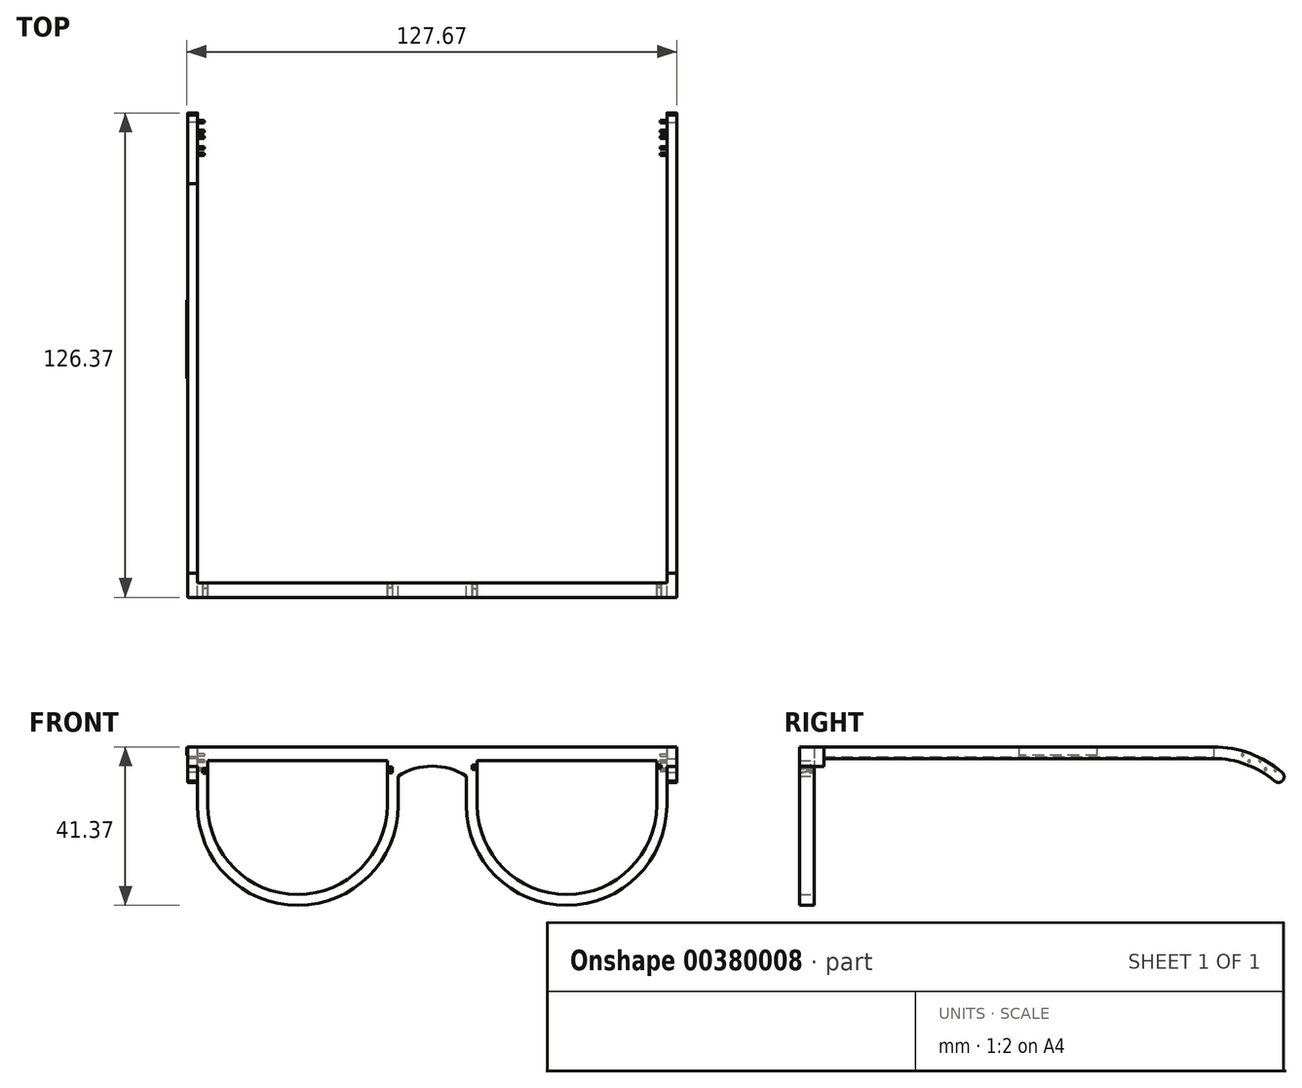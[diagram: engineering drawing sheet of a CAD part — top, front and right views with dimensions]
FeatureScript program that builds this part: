
annotation { "Feature Type Name" : "Feature", "Feature Type Description" : "" }
export const myFeature = defineFeature(function(context is Context, id is Id, definition is map)
    precondition{}
    {
        {
            var Q0;
            Q0=qCreatedBy(makeId("Front.planeOp"),FACE);
            var sketch = newSketch(context, id + "F0", { "sketchPlane" : qUnion([Q0])});
            skLineSegment(sketch, "E0.MirrorCS", {"start": v(0, 35.5) * mm, "end": v(-61.17, 35.5) * mm});
            skArc(sketch, "E1.MirrorCS", {"start": v(-8.9, 20.26) * mm, "mid": v(-35.03, -5.88) * mm, "end": v(-61.17, 20.26) * mm});
            skLineSegment(sketch, "E2.MirrorCS", {"start": v(-61.17, 35.5) * mm, "end": v(-61.17, 20.26) * mm});
            skArc(sketch, "E3", {"start": v(-58.5, 20.26) * mm, "mid": v(-35.1, -3.04) * mm, "end": v(-11.7, 20.26) * mm});
            skLineSegment(sketch, "E4", {"start": v(-58.5, 20.26) * mm, "end": v(-58.5, 31.95) * mm});
            skLineSegment(sketch, "E5", {"start": v(-58.5, 31.95) * mm, "end": v(-11.7, 31.95) * mm});
            skLineSegment(sketch, "E6", {"start": v(-11.7, 31.95) * mm, "end": v(-11.7, 20.26) * mm});
            skLineSegment(sketch, "E7.MirrorCS", {"start": v(0, 35.5) * mm, "end": v(61.17, 35.5) * mm});
            skLineSegment(sketch, "E8.MirrorCS", {"start": v(58.5, 31.95) * mm, "end": v(11.7, 31.95) * mm});
            skArc(sketch, "E9.MirrorCS", {"start": v(58.5, 20.26) * mm, "mid": v(35.1, -3.04) * mm, "end": v(11.7, 20.26) * mm});
            skArc(sketch, "E10.MirrorCS", {"start": v(8.9, 20.26) * mm, "mid": v(35.03, -5.88) * mm, "end": v(61.17, 20.26) * mm});
            skLineSegment(sketch, "E11.MirrorCS", {"start": v(61.17, 35.5) * mm, "end": v(61.17, 20.26) * mm});
            skLineSegment(sketch, "E12.MirrorCS", {"start": v(58.5, 20.26) * mm, "end": v(58.5, 31.95) * mm});
            skLineSegment(sketch, "E13", {"start": v(11.7, 20.26) * mm, "end": v(11.7, 31.95) * mm});
            skLineSegment(sketch, "E14", {"start": v(-8.9, 20.26) * mm, "end": v(-8.9, 35.5) * mm});
            skLineSegment(sketch, "E15", {"start": v(8.9, 20.26) * mm, "end": v(8.9, 35.5) * mm});
            skArc(sketch, "E16", {"start": v(8.9, 27.88) * mm, "mid": v(0, 30.44) * mm, "end": v(-8.9, 27.88) * mm});
            skSolve(sketch);
        }
        {
            var Q0;
            Q0 = qSketchRegion(id + "F0", true);
            extrude(context, id + "F1", {"entities" : qUnion([Q0]), "depth" : 3.8 * mm});
        }
        {
            var Q0;
            Q0=makeQuery(id+"F1.opExtrude","SWEPT_FACE",FACE,{"disambiguationData":[OSD([sQuery(id+"F0.wireOp",EDGE,"E11.MirrorCS")])]});
            var sketch = newSketch(context, id + "F2", { "sketchPlane" : qUnion([Q0])});
            skLineSegment(sketch, "E17.bottom", {"start": v(-3.81, 35.5) * mm, "end": v(2.54, 35.5) * mm});
            skLineSegment(sketch, "E17.top", {"start": v(-3.81, 30.41) * mm, "end": v(2.54, 30.41) * mm});
            skLineSegment(sketch, "E17.left", {"start": v(-3.81, 35.5) * mm, "end": v(-3.81, 30.41) * mm});
            skLineSegment(sketch, "E17.right", {"start": v(2.54, 35.5) * mm, "end": v(2.54, 30.41) * mm});
            skSolve(sketch);
        }
        {
            var Q0;
            Q0 = qSketchRegion(id + "F2", true);
            extrude(context, id + "F3", {"entities" : qUnion([Q0]), "depth" : 2.54 * mm});
        }
        {
            var Q0;
            Q0=makeQuery(id+"F3.opExtrude","SWEPT_BODY",BODY,{"disambiguationData":[OSD([sQuery(id+"F2.wireOp",EDGE,"E17.bottom"),sQuery(id+"F2.wireOp",EDGE,"E17.top"),sQuery(id+"F2.wireOp",EDGE,"E17.left"),sQuery(id+"F2.wireOp",EDGE,"E17.right")])]});
            var Q1;
            Q1=qCreatedBy(makeId("Right.planeOp"),FACE);
            mirror(context, id + "F4", {"operationType" : NewBodyOperationType.ADD, "entities" : qUnion([Q0]), "mirrorPlane" : qUnion([Q1])});
        }
        {
            var Q0;
            Q0=makeQuery(id+"F3.opExtrude","CAP_FACE",FACE,{"disambiguationData":[OSD([sQuery(id+"F2.wireOp",EDGE,"E17.bottom"),sQuery(id+"F2.wireOp",EDGE,"E17.top"),sQuery(id+"F2.wireOp",EDGE,"E17.left"),sQuery(id+"F2.wireOp",EDGE,"E17.right")])],"isStart":false});
            var sketch = newSketch(context, id + "F5", { "sketchPlane" : qUnion([Q0])});
            skLineSegment(sketch, "E18.bottom", {"start": v(2.54, 35.5) * mm, "end": v(104.14, 35.5) * mm});
            skLineSegment(sketch, "E18.top", {"start": v(2.54, 32.44) * mm, "end": v(104.14, 32.44) * mm});
            skLineSegment(sketch, "E18.left", {"start": v(2.54, 35.5) * mm, "end": v(2.54, 32.44) * mm});
            skLineSegment(sketch, "E18.right", {"start": v(104.14, 35.5) * mm, "end": v(104.14, 32.44) * mm});
            skSolve(sketch);
        }
        {
            var Q0;
            Q0 = qSketchRegion(id + "F5", true);
            extrude(context, id + "F6", {"entities" : qUnion([Q0]), "oppositeDirection" : true, "depth" : 2.54 * mm});
        }
        {
            var Q0;
            Q0=makeQuery(id+"F4.opPattern","COPY",FACE,{"derivedFrom":makeQuery(id+"F3.opExtrude","CAP_FACE",FACE,{"disambiguationData":[OSD([sQuery(id+"F2.wireOp",EDGE,"E17.bottom"),sQuery(id+"F2.wireOp",EDGE,"E17.top"),sQuery(id+"F2.wireOp",EDGE,"E17.left"),sQuery(id+"F2.wireOp",EDGE,"E17.right")])],"isStart":false}),"instanceName":"1"});
            var sketch = newSketch(context, id + "F7", { "sketchPlane" : qUnion([Q0])});
            skPoint(sketch, "E19.oppositeSnap0", {"position": v(-2.54, 32.95) * mm});
            skLineSegment(sketch, "E19.bottom", {"start": v(-2.54, 35.5) * mm, "end": v(-104.14, 35.5) * mm});
            skLineSegment(sketch, "E19.top", {"start": v(-2.54, 32.95) * mm, "end": v(-104.14, 32.95) * mm});
            skLineSegment(sketch, "E19.left", {"start": v(-2.54, 35.5) * mm, "end": v(-2.54, 32.95) * mm});
            skLineSegment(sketch, "E19.right", {"start": v(-104.14, 35.5) * mm, "end": v(-104.14, 32.95) * mm});
            skSolve(sketch);
        }
        {
            var Q0;
            Q0 = qSketchRegion(id + "F7", true);
            extrude(context, id + "F8", {"entities" : qUnion([Q0]), "oppositeDirection" : true, "depth" : 2.54 * mm});
        }
        {
            var Q0;
            Q0=makeQuery(id+"F8.opExtrude","CAP_FACE",FACE,{"disambiguationData":[OSD([sQuery(id+"F7.wireOp",EDGE,"E19.bottom"),sQuery(id+"F7.wireOp",EDGE,"E19.top"),sQuery(id+"F7.wireOp",EDGE,"E19.left"),sQuery(id+"F7.wireOp",EDGE,"E19.right")])],"isStart":true});
            var sketch = newSketch(context, id + "F9", { "sketchPlane" : qUnion([Q0])});
            skLineSegment(sketch, "E20.bottom", {"start": v(-73.76, 35.29) * mm, "end": v(-53.34, 35.29) * mm});
            skLineSegment(sketch, "E20.top", {"start": v(-73.76, 33.34) * mm, "end": v(-53.34, 33.34) * mm});
            skLineSegment(sketch, "E20.left", {"start": v(-73.76, 35.29) * mm, "end": v(-73.76, 33.34) * mm});
            skLineSegment(sketch, "E20.right", {"start": v(-53.34, 35.29) * mm, "end": v(-53.34, 33.34) * mm});
            skPoint(sketch, "E21", {"position": v(-53.34, 32.95) * mm});
            skSolve(sketch);
        }
        {
            var Q0;
            Q0 = qSketchRegion(id + "F9", true);
            extrude(context, id + "F10", {"entities" : qUnion([Q0]), "depth" : 0.25 * mm});
        }
        {
            var Q0;
            Q0=makeQuery(id+"F6.opExtrude","CAP_FACE",FACE,{"disambiguationData":[OSD([sQuery(id+"F5.wireOp",EDGE,"E18.bottom"),sQuery(id+"F5.wireOp",EDGE,"E18.top"),sQuery(id+"F5.wireOp",EDGE,"E18.left"),sQuery(id+"F5.wireOp",EDGE,"E18.right")])],"isStart":true});
            var sketch = newSketch(context, id + "F11", { "sketchPlane" : qUnion([Q0])});
            skArc(sketch, "E22", {"start": v(120.08, 26.59) * mm, "mid": v(112.63, 30.93) * mm, "end": v(104.14, 32.44) * mm});
            skArc(sketch, "E23", {"start": v(122, 28.86) * mm, "mid": v(113.67, 33.78) * mm, "end": v(104.14, 35.5) * mm});
            skArc(sketch, "E24", {"start": v(120.08, 26.59) * mm, "mid": v(122.21, 26.73) * mm, "end": v(122, 28.86) * mm});
            skSolve(sketch);
        }
        {
            var Q0;
            Q0=makeQuery(id+"F11.imprint","IMPRINT",FACE,{"disambiguationData":[TD([[makeQuery(id+"F11.imprint","IMPRINT",EDGE,{"derivedFrom":sQuery(id+"F11.wireOp",EDGE,"E22")}),-1.0]])]});
            extrude(context, id + "F12", {"entities" : qUnion([Q0]), "operationType" : NewBodyOperationType.ADD, "oppositeDirection" : true, "depth" : 2.54 * mm});
        }
        {
            var Q0;
            Q0=makeQuery(id+"F6.opExtrude","SWEPT_BODY",BODY,{"disambiguationData":[OSD([sQuery(id+"F5.wireOp",EDGE,"E18.bottom"),sQuery(id+"F5.wireOp",EDGE,"E18.top"),sQuery(id+"F5.wireOp",EDGE,"E18.left"),sQuery(id+"F5.wireOp",EDGE,"E18.right")])]});
            var Q1;
            Q1=qCreatedBy(makeId("Right.planeOp"),FACE);
            mirror(context, id + "F13", {"entities" : qUnion([Q0]), "mirrorPlane" : qUnion([Q1])});
        }
        {
            var Q0;
            {var subQ0=sQuery(id+"F5.wireOp",EDGE,"E18.right");Q0=makeQuery(id+"F12.boolean.opBoolean","MERGE",FACE,{"derivedFrom":[makeQuery(id+"F6.opExtrude","CAP_FACE",FACE,{"disambiguationData":[OSD([sQuery(id+"F5.wireOp",EDGE,"E18.bottom"),sQuery(id+"F5.wireOp",EDGE,"E18.top"),sQuery(id+"F5.wireOp",EDGE,"E18.left"),subQ0])],"isStart":false}),makeQuery(id+"F12.opExtrude","CAP_FACE",FACE,{"disambiguationData":[OSD([subQ0,sQuery(id+"F11.wireOp",EDGE,"E22"),sQuery(id+"F11.wireOp",EDGE,"E23"),sQuery(id+"F11.wireOp",EDGE,"E24")])],"isStart":false})]});}
            var sketch = newSketch(context, id + "F14", { "sketchPlane" : qUnion([Q0])});
            skCircle(sketch, "E25", {"center": v(-120.27, 29.4) * mm, "radius": 0.32 * mm});
            skCircle(sketch, "E26", {"center": v(-117.71, 29.7) * mm, "radius": 0.32 * mm});
            skCircle(sketch, "E27", {"center": v(-116.28, 31.89) * mm, "radius": 0.32 * mm});
            skCircle(sketch, "E28", {"center": v(-113.44, 31.77) * mm, "radius": 0.32 * mm});
            skCircle(sketch, "E29", {"center": v(-111.73, 33.4) * mm, "radius": 0.32 * mm});
            skSolve(sketch);
        }
        {
            var Q0;
            Q0 = qSketchRegion(id + "F14", true);
            extrude(context, id + "F15", {"entities" : qUnion([Q0]), "depth" : 1.78 * mm});
        }
        {
            var Q0;
            Q0=makeQuery(id+"F15.opExtrude","SWEPT_BODY",BODY,{"disambiguationData":[OSD([sQuery(id+"F14.wireOp",EDGE,"E28")])]});
            var Q1;
            Q1=makeQuery(id+"F15.opExtrude","SWEPT_BODY",BODY,{"disambiguationData":[OSD([sQuery(id+"F14.wireOp",EDGE,"E29")])]});
            var Q2;
            Q2=makeQuery(id+"F15.opExtrude","SWEPT_BODY",BODY,{"disambiguationData":[OSD([sQuery(id+"F14.wireOp",EDGE,"E26")])]});
            var Q3;
            Q3=makeQuery(id+"F15.opExtrude","SWEPT_BODY",BODY,{"disambiguationData":[OSD([sQuery(id+"F14.wireOp",EDGE,"E25")])]});
            var Q4;
            Q4=makeQuery(id+"F15.opExtrude","SWEPT_BODY",BODY,{"disambiguationData":[OSD([sQuery(id+"F14.wireOp",EDGE,"E27")])]});
            var Q5;
            Q5=qCreatedBy(makeId("Right.planeOp"),FACE);
            mirror(context, id + "F16", {"operationType" : NewBodyOperationType.ADD, "entities" : qUnion([Q0, Q1, Q2, Q3, Q4]), "mirrorPlane" : qUnion([Q5])});
        }
        {
            var Q0;
            Q0=makeQuery(id+"F1.opExtrude","SWEPT_FACE",FACE,{"disambiguationData":[OSD([sQuery(id+"F0.wireOp",EDGE,"E12.MirrorCS")])]});
            var sketch = newSketch(context, id + "F17", { "sketchPlane" : qUnion([Q0])});
            skCircle(sketch, "E30", {"center": v(0.9, 30.36) * mm, "radius": 0.4 * mm});
            skLineSegment(sketch, "E31", {"start": v(3.81, 30.76) * mm, "end": v(3.81, 29.96) * mm});
            skLineSegment(sketch, "E32", {"start": v(1.24, 30.58) * mm, "end": v(3.81, 30.76) * mm});
            skLineSegment(sketch, "E33", {"start": v(3.81, 29.96) * mm, "end": v(1.28, 30.24) * mm});
            skSolve(sketch);
        }
        {
            var Q0;
            Q0 = qSketchRegion(id + "F17", true);
            extrude(context, id + "F18", {"entities" : qUnion([Q0]), "operationType" : NewBodyOperationType.REMOVE, "oppositeDirection" : true, "depth" : 1.14 * mm});
        }
        {
            var Q0;
            Q0=makeQuery(id+"F1.opExtrude","SWEPT_FACE",FACE,{"disambiguationData":[OSD([sQuery(id+"F0.wireOp",EDGE,"E13")])]});
            var sketch = newSketch(context, id + "F19", { "sketchPlane" : qUnion([Q0])});
            skCircle(sketch, "E34", {"center": v(-0.95, 30.12) * mm, "radius": 0.62 * mm});
            skLineSegment(sketch, "E35", {"start": v(-1.47, 30.46) * mm, "end": v(-3.81, 30.8) * mm});
            skLineSegment(sketch, "E36", {"start": v(-3.81, 30.8) * mm, "end": v(-3.81, 29.6) * mm});
            skLineSegment(sketch, "E37", {"start": v(-3.81, 29.6) * mm, "end": v(-1.53, 29.9) * mm});
            skSolve(sketch);
        }
        {
            var Q0;
            Q0 = qSketchRegion(id + "F19", true);
            extrude(context, id + "F20", {"entities" : qUnion([Q0]), "operationType" : NewBodyOperationType.REMOVE, "oppositeDirection" : true, "depth" : 1.27 * mm});
        }
        {
            var Q0;
            Q0=makeQuery(id+"F1.opExtrude","SWEPT_FACE",FACE,{"disambiguationData":[OSD([sQuery(id+"F0.wireOp",EDGE,"E4")])]});
            var sketch = newSketch(context, id + "F21", { "sketchPlane" : qUnion([Q0])});
            skCircle(sketch, "E38", {"center": v(-0.81, 29.35) * mm, "radius": 0.62 * mm});
            skLineSegment(sketch, "E39", {"start": v(-1.4, 29.55) * mm, "end": v(-3.81, 29.9) * mm});
            skLineSegment(sketch, "E40", {"start": v(-3.81, 29.9) * mm, "end": v(-3.81, 28.53) * mm});
            skLineSegment(sketch, "E41", {"start": v(-3.81, 28.53) * mm, "end": v(-1.36, 29.07) * mm});
            skSolve(sketch);
        }
        {
            var Q0;
            Q0 = qSketchRegion(id + "F21", true);
            extrude(context, id + "F22", {"entities" : qUnion([Q0]), "operationType" : NewBodyOperationType.REMOVE, "oppositeDirection" : true, "depth" : 1.27 * mm});
        }
        {
            var Q0;
            Q0=makeQuery(id+"F1.opExtrude","SWEPT_FACE",FACE,{"disambiguationData":[OSD([sQuery(id+"F0.wireOp",EDGE,"E6")])]});
            var sketch = newSketch(context, id + "F23", { "sketchPlane" : qUnion([Q0])});
            skCircle(sketch, "E42", {"center": v(0.8, 29.55) * mm, "radius": 0.64 * mm});
            skLineSegment(sketch, "E43", {"start": v(1.39, 29.8) * mm, "end": v(3.81, 30.28) * mm});
            skLineSegment(sketch, "E44", {"start": v(1.34, 29.21) * mm, "end": v(3.81, 28.75) * mm});
            skLineSegment(sketch, "E45", {"start": v(3.81, 28.75) * mm, "end": v(3.81, 30.28) * mm});
            skSolve(sketch);
        }
        {
            var Q0;
            Q0 = qSketchRegion(id + "F23", true);
            extrude(context, id + "F24", {"entities" : qUnion([Q0]), "operationType" : NewBodyOperationType.REMOVE, "oppositeDirection" : true, "depth" : 1.27 * mm});
        }
    });
